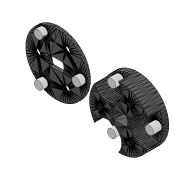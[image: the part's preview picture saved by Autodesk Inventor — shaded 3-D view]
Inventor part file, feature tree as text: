
AUTODESK INVENTOR PART (.ipt)
format: ipt  version: 2022 (Build 260153000, 153)  size: 220,160 bytes
history: native  units: mm
features: extrude x2, sketch x2, other x1
ambient origin geometry x8: Origin, YZ Plane, XZ Plane, XY Plane, X Axis, Y Axis, Z Axis, Center Point
bodies: Volumenkörper1 (feature_tree)
feature tree (5):
  extrude  "Extrusion1"  Depth=3.0mm
  extrude  "Extrusion2"  Depth=3.0mm TaperAngle=0.0deg
  sketch  "Skizze1"  dims[d0=3.0mm d1=3.0mm]
  sketch  "Skizze2"  dims[d2=3.0mm d3=3.0mm d4=0.0mm d5=3.0mm d6=3.0mm d7=3.0mm d8=2.0mm d9=0.0mm]
  other  "MeshFeature1"
